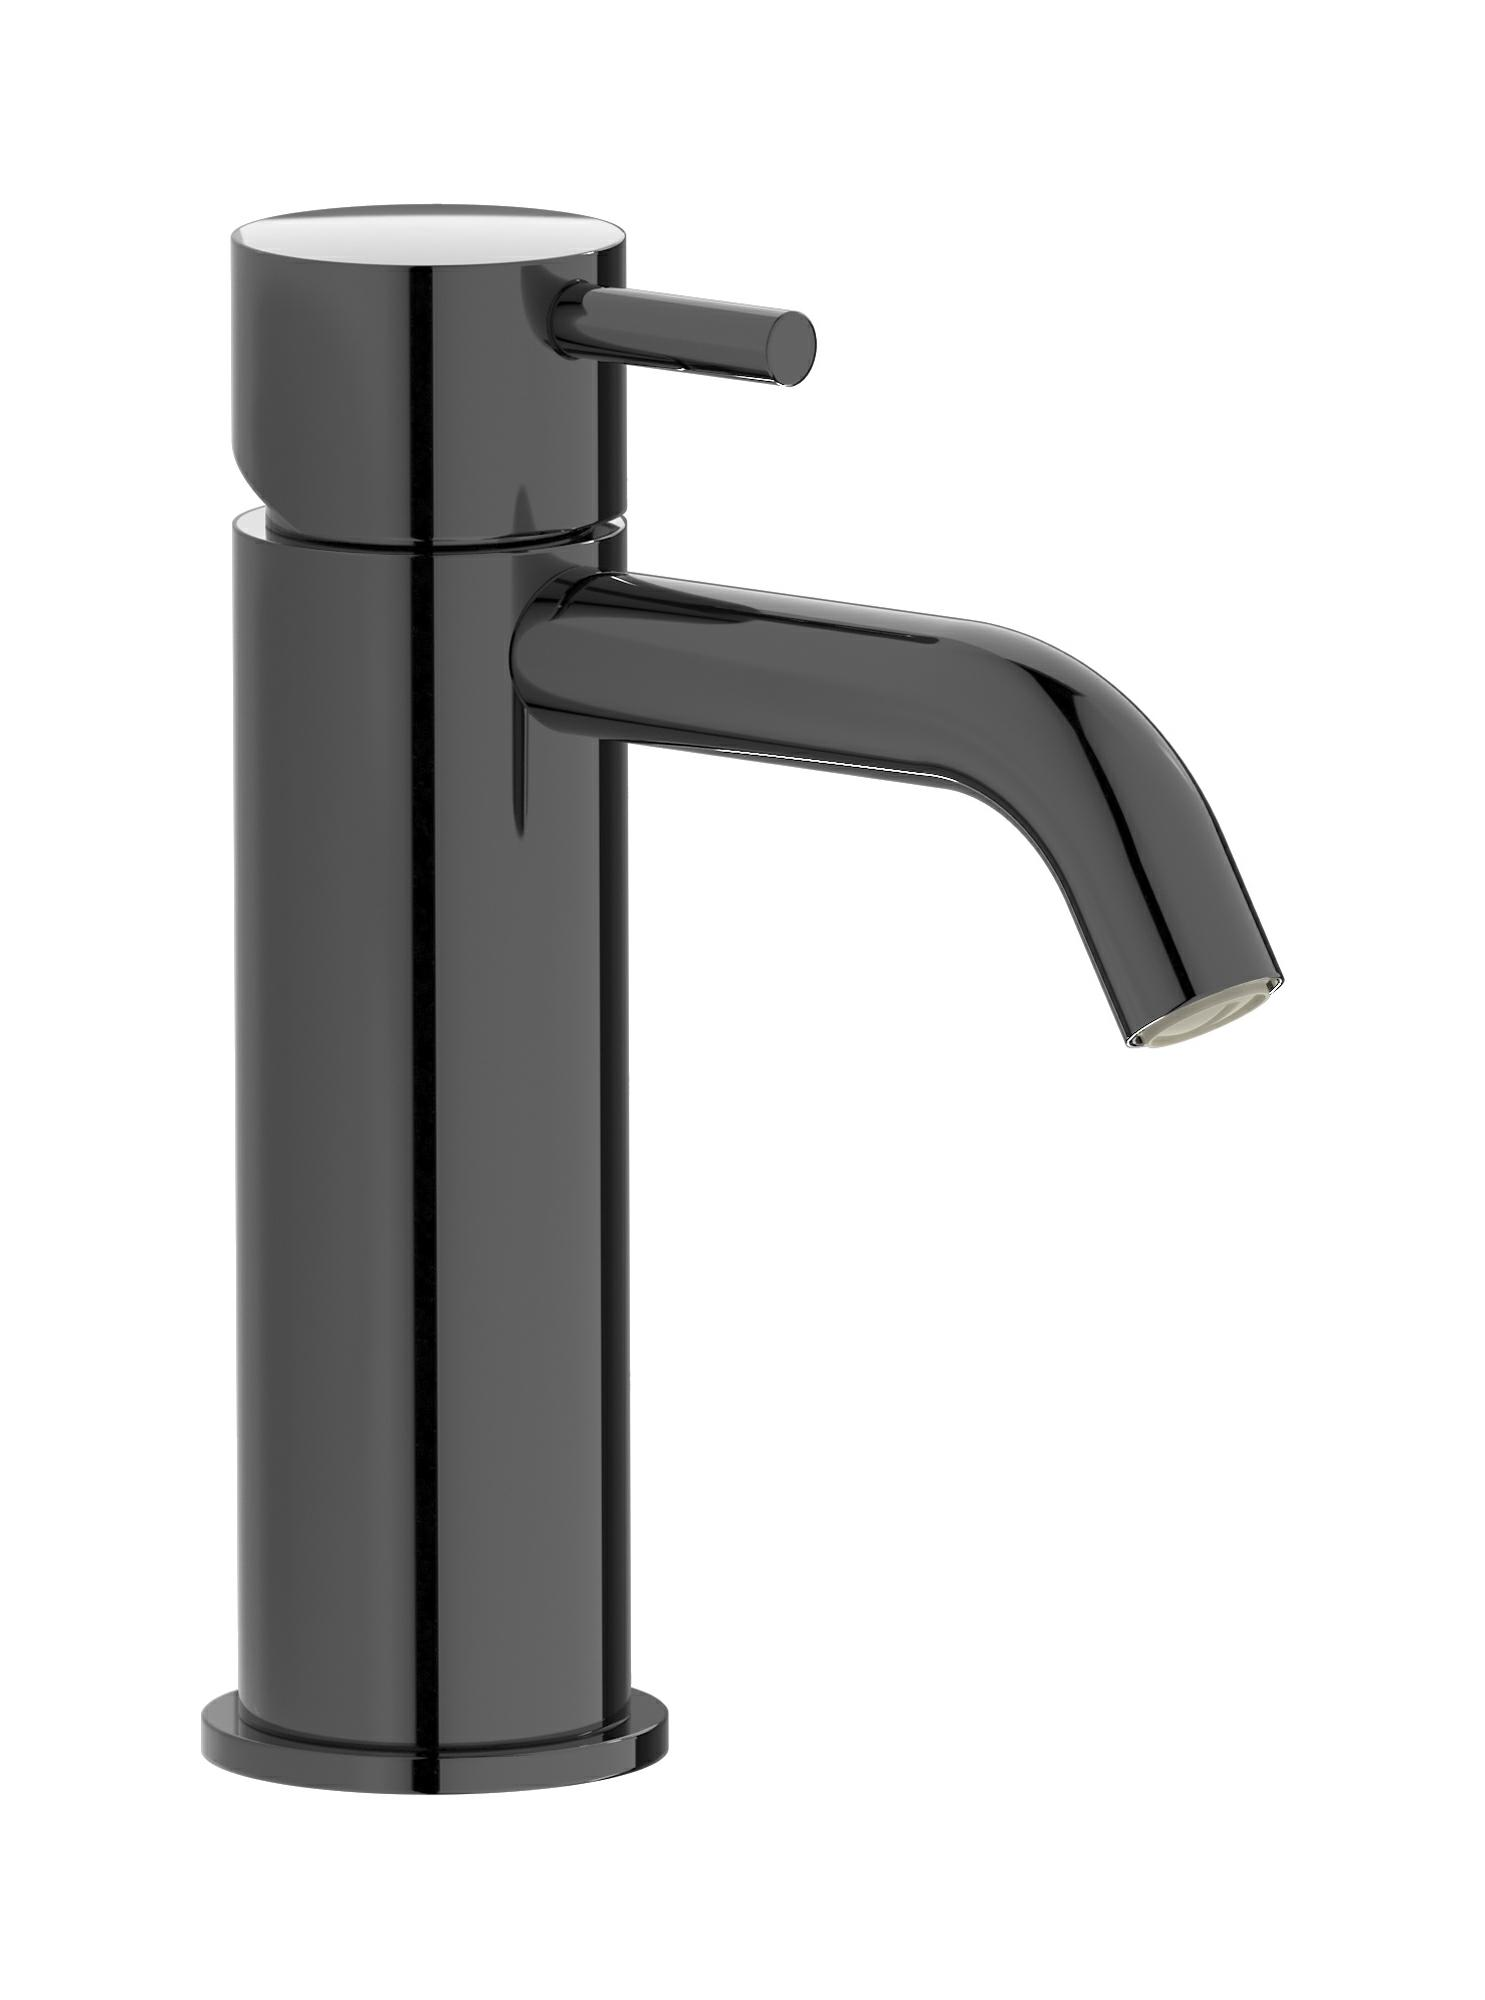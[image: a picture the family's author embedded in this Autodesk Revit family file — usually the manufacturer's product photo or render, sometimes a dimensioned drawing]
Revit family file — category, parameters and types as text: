
# Revit family: MT200
name_source: partatom
category: Apparecchi idraulici
units: mm (PartAtom-declared; Revit-internal decimal feet)

## family parameters
Basato su piano di lavoro = No
Condiviso = No
Mantieni orientamento annotazione = No
Numero OmniClass = 23.45.55.17
Punto di calcolo locali = No
Quota connettore circolare = Usa diametro
Sempre verticale = Sì
Taglio con vuoti quando caricato = No
Tipo di parte = Normale
Titolo OmniClass = Mixing Faucets

## types (13) — shared parameters
Cold water inlet = 10 mm  [stored 0.0328084 ft]
Commenti sul tipo = Washbasin mixer
Connessione CW = No
Connessione HW = No
Connessione di scarico = No
Connessione di ventilazione = No
Descrizione = Monohole washbasin mixer complete with drain
Hot water inlet = 10 mm  [stored 0.0328084 ft]
Produttore = IB Rubinetterie S.p.A.
URL = https://www.weareib.it
zero-valued in all types: Prospetto di default

## per-type parameters (varying)
| type | Finishes surface | Immagine tipo | Modello |
| Chrome | IB_Chrome | MT200CC.jpg | MT200CC |
| Brushed nickel | IB_Brushed nickel | MT200SS.jpg | MT200SS |
| Natural brass | IB_Brass | MT200ON.jpg | MT200ON |
| Matt white | IB_matt white | MT200BO.jpg | MT200BO |
| Matt black | IB_matt black | MT200NP.jpg | MT200NP |
| Black chrome | IB_Black chrome | MT200CF.jpg | MT200CF |
| Brushed black chrome | IB_Brushed black chrome | MT200CS.jpg | MT200CS |
| Pale gold | IB_Pale gold | MT200II.jpg | MT200II |
| Brushed pale gold | IB_brushed pale gold | MT200IS.jpg | MT200IS |
| Rose gold | IB_Rose gold | MT200RS.jpg | MT200RS |
| Brushed rose gold | IB_Brushed rose gold | MT200SR.jpg | MT200SR |
| Gold | IB_gold | MT200OO.jpg | MT200OO |
| Brushed gold | IB_brushed gold | MT200OS.jpg | MT200OS |

note: [stored X ft] marks values corroborated as IEEE doubles in the binary element streams (Revit-internal decimal feet)
